# Revit family: 2014-ES_Puerta-Batiente-Automatica-2-Hojas_AEPA_XXx
name_source: partatom
category: Puertas
revit_build: Autodesk Revit 2014 (Build: 20130308_1515(x64)
units: mm (PartAtom-declared; Revit-internal decimal feet)

## types (1)
- 2014-ES_Puerta-Batiente-Automatica-2-Hojas_AEPA_XXx
    Altura = 1600 mm  [stored 5.24934 ft]
    Altura CONTROL = 1600 mm  [stored 5.24934 ft]
    Anchura = 2400 mm
    Anchura CONTROL = 2400 mm
    Anchura bisagra a centro = 1175 mm
    Asociación - AEPA = http://www.aepa.ws
    Bimetica = http://www.bimetica.com
    Cierre de muro = Por anfitrión
    Colección = Biblioteca BIM AEPA
    Creado por = Bimetica Parametric Design Services S.L.
    Descripción = Puerta Bateinte Automatica
    Desfase exterior = 0 mm  [stored 0 ft]
    Fabricante - CONTROLSA = http://www.controlsa.com
    Fabricante - PUERTAS BAHÍA = http://www.puertasbahia.com
    Fabricante - ROLLTORE PORTIS = http://www.portis.es
    Fecha Revisión de Contenido = 29/12/2014
    Fecha de Caducidad de Información = 01/01/2016
    Función = Interior
    Grosor = 70 mm
    Lama ACABADO = 235 mm  [stored 0.770997 ft]
    Masterformat Código = 08 71 13
    Masterformat Descripción = Automatic Door Operators
    Material Brazos = Acero sin pintar - Puerta Generaica AEPA
    Material Estructura y Bisagras = Acero - Puerta Generica - AEPA
    Material Lamas de acabado = Panel Madera Roble acabado - Puerta Generica AEPA
    Material Piezas moviles = Gomas blancas - Puerta Generica- AEPA
    Material cubierta Mecanismo = Plastico Solido- Puerta Generica- AEPA
    Modelo = Generico AEPA
    Omniclass Código = 23-17 19 11 11
    Omniclass Título = Rotation, Pivoting Door Gear
    UNSPSC Categoría = Automatic doors
    UNSPSC Código = 30171510
    URL = http://www.aepa.ws
    Uniclass 2.0 Código = 75-30-26-05
    Uniclass 2.0 Descripción = Automatic gate opening devices

note: [stored X ft] marks values corroborated as IEEE doubles in the binary element streams (Revit-internal decimal feet)
